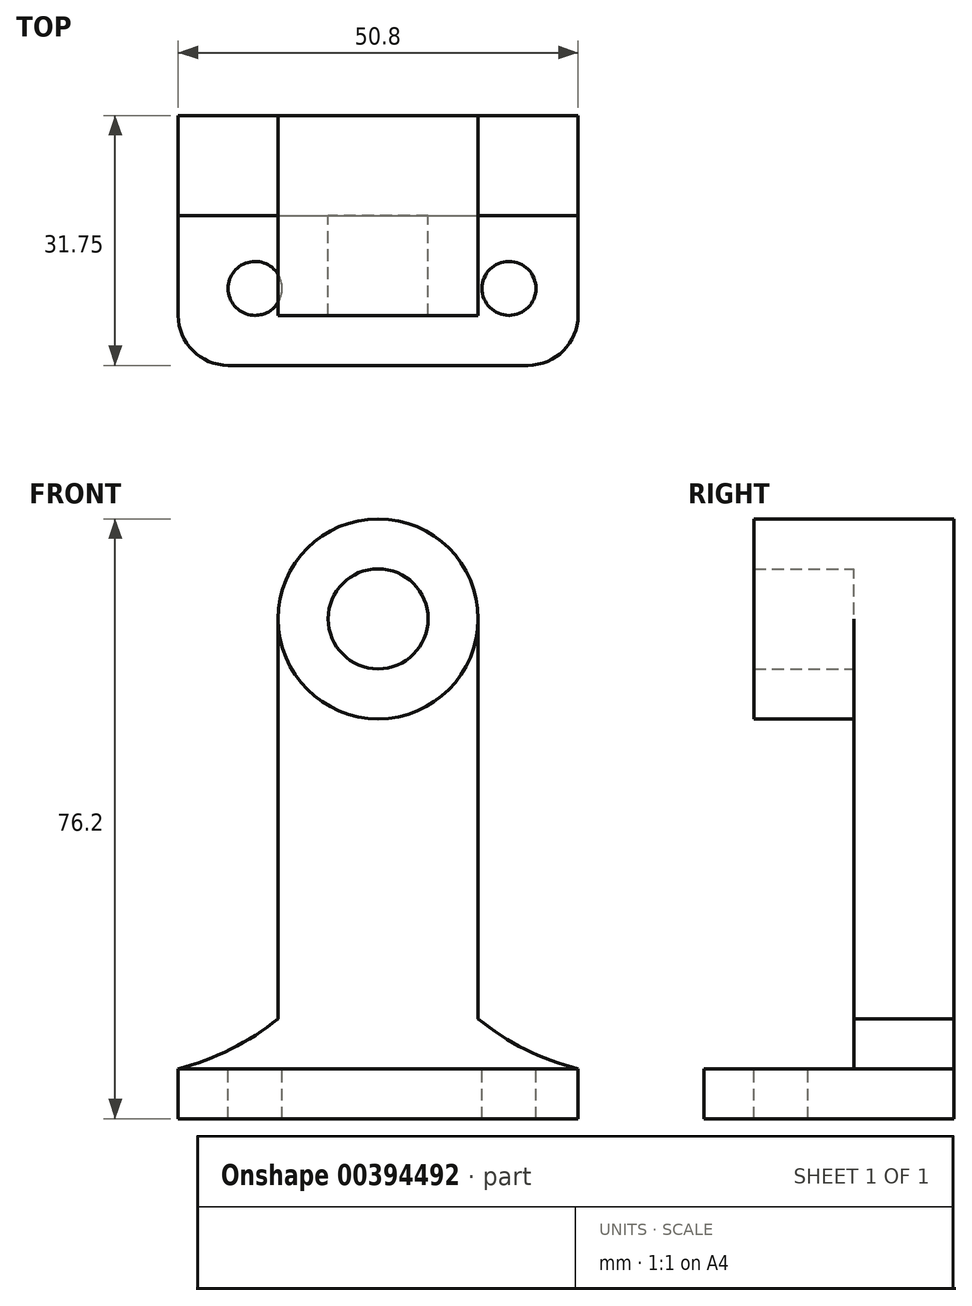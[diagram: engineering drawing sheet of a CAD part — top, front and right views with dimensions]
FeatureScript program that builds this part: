
annotation { "Feature Type Name" : "Feature", "Feature Type Description" : "" }
export const myFeature = defineFeature(function(context is Context, id is Id, definition is map)
    precondition{}
    {
        {
            var Q0;
            Q0=qCreatedBy(makeId("Front.planeOp"),FACE);
            var sketch = newSketch(context, id + "F0", { "sketchPlane" : qUnion([Q0])});
            skLineSegment(sketch, "E0.bottom", {"start": v(0, -23.51) * mm, "end": v(-50.8, -23.51) * mm});
            skLineSegment(sketch, "E0.top", {"start": v(0, 52.69) * mm, "end": v(-50.8, 52.69) * mm});
            skLineSegment(sketch, "E0.left", {"start": v(0, -23.51) * mm, "end": v(0, 52.69) * mm});
            skLineSegment(sketch, "E0.right", {"start": v(-50.8, -23.51) * mm, "end": v(-50.8, 52.69) * mm});
            skSolve(sketch);
        }
        {
            var Q0;
            Q0=makeQuery(id+"F0.imprint","IMPRINT",FACE,{"disambiguationData":[TD([[makeQuery(id+"F0.imprint","IMPRINT",EDGE,{"derivedFrom":sQuery(id+"F0.wireOp",EDGE,"E0.bottom")}),-1.0]])]});
            extrude(context, id + "F1", {"entities" : qUnion([Q0]), "depth" : 31.75 * mm});
        }
        {
            var Q0;
            Q0=makeQuery(id+"F1.opExtrude","SWEPT_FACE",FACE,{"disambiguationData":[OSD([sQuery(id+"F0.wireOp",EDGE,"E0.left")])]});
            var sketch = newSketch(context, id + "F2", { "sketchPlane" : qUnion([Q0])});
            skLineSegment(sketch, "E1", {"start": v(-12.7, 52.69) * mm, "end": v(-31.75, 52.69) * mm});
            skLineSegment(sketch, "E2", {"start": v(-31.75, 52.69) * mm, "end": v(-31.75, -17.16) * mm});
            skLineSegment(sketch, "E3", {"start": v(-31.75, -17.16) * mm, "end": v(-12.7, -17.16) * mm});
            skLineSegment(sketch, "E4", {"start": v(-12.7, -17.16) * mm, "end": v(-12.7, 52.69) * mm});
            skSolve(sketch);
        }
        {
            var Q0;
            Q0=makeQuery(id+"F2.imprint","IMPRINT",FACE,{"disambiguationData":[TD([[makeQuery(id+"F2.imprint","IMPRINT",EDGE,{"derivedFrom":sQuery(id+"F2.wireOp",EDGE,"E1")}),-1.0]])]});
            extrude(context, id + "F3", {"entities" : qUnion([Q0]), "operationType" : NewBodyOperationType.REMOVE, "oppositeDirection" : true, "depth" : 50.8 * mm});
        }
        {
            var Q0;
            Q0=makeQuery(id+"F3.boolean.opBoolean","COPY",FACE,{"derivedFrom":makeQuery(id+"F3.opExtrude","SWEPT_FACE",FACE,{"disambiguationData":[OSD([sQuery(id+"F2.wireOp",EDGE,"E4")])]})});
            var sketch = newSketch(context, id + "F4", { "sketchPlane" : qUnion([Q0])});
            skArc(sketch, "E5", {"start": v(-12.7, -10.81) * mm, "mid": v(-6.71, -14.71) * mm, "end": v(0, -17.16) * mm});
            skArc(sketch, "E6", {"start": v(-50.8, -17.16) * mm, "mid": v(-44.1, -14.67) * mm, "end": v(-38.1, -10.81) * mm});
            skLineSegment(sketch, "E7", {"start": v(-38.1, -10.81) * mm, "end": v(-38.1, 52.69) * mm});
            skLineSegment(sketch, "E8", {"start": v(-38.1, 52.69) * mm, "end": v(-50.8, 52.69) * mm});
            skLineSegment(sketch, "E9", {"start": v(-50.8, 52.69) * mm, "end": v(-50.8, -17.16) * mm});
            skLineSegment(sketch, "E10", {"start": v(-12.7, -10.81) * mm, "end": v(-12.7, 52.69) * mm});
            skLineSegment(sketch, "E11", {"start": v(-12.7, 52.69) * mm, "end": v(0, 52.69) * mm});
            skLineSegment(sketch, "E12", {"start": v(0, 52.69) * mm, "end": v(0, -17.16) * mm});
            skSolve(sketch);
        }
        {
            var Q0;
            Q0=makeQuery(id+"F4.imprint","IMPRINT",FACE,{"disambiguationData":[TD([[makeQuery(id+"F4.imprint","IMPRINT",EDGE,{"derivedFrom":sQuery(id+"F4.wireOp",EDGE,"E6")}),1.0]])]});
            var Q1;
            Q1=makeQuery(id+"F4.imprint","IMPRINT",FACE,{"disambiguationData":[TD([[makeQuery(id+"F4.imprint","IMPRINT",EDGE,{"derivedFrom":sQuery(id+"F4.wireOp",EDGE,"E5")}),1.0]])]});
            extrude(context, id + "F5", {"entities" : qUnion([Q0, Q1]), "operationType" : NewBodyOperationType.REMOVE, "oppositeDirection" : true, "depth" : 25.4 * mm});
        }
        {
            var Q0;
            Q0=makeQuery(id+"F3.boolean.opBoolean","COPY",FACE,{"derivedFrom":makeQuery(id+"F3.opExtrude","SWEPT_FACE",FACE,{"disambiguationData":[OSD([sQuery(id+"F2.wireOp",EDGE,"E4")])]})});
            var sketch = newSketch(context, id + "F6", { "sketchPlane" : qUnion([Q0])});
            skPoint(sketch, "E13.centerSnap0", {"position": v(-25.4, 52.69) * mm});
            skCircle(sketch, "E14", {"center": v(-25.4, 39.99) * mm, "radius": 12.7 * mm});
            skCircle(sketch, "E15", {"center": v(-25.4, 39.99) * mm, "radius": 6.35 * mm});
            skSolve(sketch);
        }
        {
            var Q0;
            Q0=makeQuery(id+"F6.imprint","IMPRINT",FACE,{"disambiguationData":[TD([[makeQuery(id+"F6.imprint","IMPRINT",EDGE,{"derivedFrom":sQuery(id+"F6.wireOp",EDGE,"E15")}),-1.0]])]});
            extrude(context, id + "F7", {"entities" : qUnion([Q0]), "operationType" : NewBodyOperationType.ADD, "depth" : 12.7 * mm});
        }
        {
            var Q0;
            {var subQ0=makeQuery(id+"F3.boolean.opBoolean","COPY",FACE,{"derivedFrom":makeQuery(id+"F3.opExtrude","SWEPT_FACE",FACE,{"disambiguationData":[OSD([sQuery(id+"F2.wireOp",EDGE,"E4")])]})});Q0=makeQuery(id+"F7.boolean.opBoolean","SPLIT",FACE,{"disambiguationData":[TD([makeQuery(id+"F1.opExtrude","SWEPT_FACE",FACE,{"disambiguationData":[OSD([sQuery(id+"F0.wireOp",EDGE,"E0.top")])]}),subQ0,makeQuery(id+"F5.boolean.opBoolean","COPY",FACE,{"derivedFrom":makeQuery(id+"F5.opExtrude","SWEPT_FACE",FACE,{"disambiguationData":[OSD([sQuery(id+"F4.wireOp",EDGE,"E7")])]})}),makeQuery(id+"F7.opExtrude","SWEPT_FACE",FACE,{"disambiguationData":[OSD([sQuery(id+"F6.wireOp",EDGE,"E14")])]})])],"derivedFrom":subQ0});}
            var Q1;
            {var subQ0=makeQuery(id+"F3.boolean.opBoolean","COPY",FACE,{"derivedFrom":makeQuery(id+"F3.opExtrude","SWEPT_FACE",FACE,{"disambiguationData":[OSD([sQuery(id+"F2.wireOp",EDGE,"E4")])]})});Q1=makeQuery(id+"F7.boolean.opBoolean","SPLIT",FACE,{"disambiguationData":[TD([makeQuery(id+"F1.opExtrude","SWEPT_FACE",FACE,{"disambiguationData":[OSD([sQuery(id+"F0.wireOp",EDGE,"E0.top")])]}),subQ0,makeQuery(id+"F5.boolean.opBoolean","COPY",FACE,{"derivedFrom":makeQuery(id+"F5.opExtrude","SWEPT_FACE",FACE,{"disambiguationData":[OSD([sQuery(id+"F4.wireOp",EDGE,"E10")])]})}),makeQuery(id+"F7.opExtrude","SWEPT_FACE",FACE,{"disambiguationData":[OSD([sQuery(id+"F6.wireOp",EDGE,"E14")])]})])],"derivedFrom":subQ0});}
            extrude(context, id + "F8", {"entities" : qUnion([Q0, Q1]), "operationType" : NewBodyOperationType.REMOVE, "oppositeDirection" : true, "depth" : 25.4 * mm});
        }
        {
            var Q0;
            Q0=makeQuery(id+"F3.boolean.opBoolean","COPY",FACE,{"derivedFrom":makeQuery(id+"F3.opExtrude","SWEPT_FACE",FACE,{"disambiguationData":[OSD([sQuery(id+"F2.wireOp",EDGE,"E3")])]})});
            var sketch = newSketch(context, id + "F9", { "sketchPlane" : qUnion([Q0])});
            skArc(sketch, "E16", {"start": v(-6.35, -31.75) * mm, "mid": v(-1.86, -29.9) * mm, "end": v(0, -25.4) * mm});
            skArc(sketch, "E17", {"start": v(-50.8, -25.4) * mm, "mid": v(-48.94, -29.9) * mm, "end": v(-44.45, -31.75) * mm});
            skCircle(sketch, "E18", {"center": v(-41.03, -21.98) * mm, "radius": 3.42 * mm});
            skCircle(sketch, "E19", {"center": v(-8.78, -21.98) * mm, "radius": 3.42 * mm});
            skSolve(sketch);
        }
        {
            var Q0;
            Q0=makeQuery(id+"F9.imprint","IMPRINT",FACE,{"disambiguationData":[TD([[makeQuery(id+"F9.imprint","IMPRINT",EDGE,{"derivedFrom":sQuery(id+"F9.wireOp",EDGE,"E18")}),1.0]])]});
            var Q1;
            Q1=makeQuery(id+"F9.imprint","IMPRINT",FACE,{"disambiguationData":[TD([[makeQuery(id+"F9.imprint","IMPRINT",EDGE,{"derivedFrom":sQuery(id+"F9.wireOp",EDGE,"E19")}),1.0]])]});
            var Q2;
            {var subQ0=sQuery(id+"F9.wireOp",EDGE,"E17");Q2=makeQuery(id+"F9.imprint","IMPRINT",FACE,{"disambiguationData":[TD([[makeQuery(id+"F9.imprint","IMPRINT",EDGE,{"derivedFrom":subQ0}),-1.0]])]});}
            var Q3;
            {var subQ0=sQuery(id+"F9.wireOp",EDGE,"E16");Q3=makeQuery(id+"F9.imprint","IMPRINT",FACE,{"disambiguationData":[TD([[makeQuery(id+"F9.imprint","IMPRINT",EDGE,{"derivedFrom":subQ0}),-1.0]])]});}
            extrude(context, id + "F10", {"entities" : qUnion([Q0, Q1, Q2, Q3]), "operationType" : NewBodyOperationType.REMOVE, "oppositeDirection" : true, "depth" : 25.4 * mm});
        }
    });
